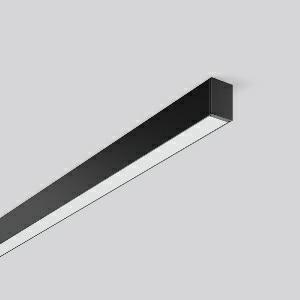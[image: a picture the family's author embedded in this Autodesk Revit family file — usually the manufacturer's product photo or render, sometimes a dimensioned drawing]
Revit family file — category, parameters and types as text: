
# Revit family: less_is_more_27_312198_003_1_76_4c85
name_source: partatom
category: Lighting Fixtures
units: mm (PartAtom-declared; Revit-internal decimal feet)

## family parameters
Cut with Voids When Loaded = No
Host = Face
Light Source = No
Part Type = Normal
Room Calculation Point = No
Round Connector Dimension = Use Diameter
Shared = No

## types (1)
- LESS IS MORE 27 (1 x LED Modul 840, 1900 lm, 4000)
    Apparent Load = 31 VA
    CIE Flux Codes = 48 79 96 100 100
    Color Rendering = 80
    Color Temperature = 4000
    Default Elevation = 1800 mm
    Description = Series: LESS IS MORE 27
Ceiling and wall luminaire with slim design. Housing: extruded aluminium profile, powder-coated. End cap aluminium powder-coated. Diffuser made of non-yellowing plastic (PMMA), opal. Suitable for Ceiling mounting, Wall (surface). External driver with connecting cable. 
Colour: deep black, matt (RAL 9005)
Length: 1212 mm
Width: 28 mm
Height: 38 mm
Lamp: LED
Socket: without socket
Colour temperature: 4000K
Colour rendering index (CRI): 82
System power: 31 W
Rated luminous flux: 1900 lm
Luminous efficiency: 61 lm/W
Control gear: Voltage converter, DALI dim.
Protection class: II
Type of protection: IP 20
    Height = 38 mm
    Lamp = 1 x LED Modul 840
    Lamp Light Flux = 1900 lm
    Lamp count = 1
    Length = 1212 mm
    Lifetime = 50000 h
    Luminous efficacy = 61 lm/W
    Manufacturer = RZB
    ModVariant = No
    Model = 312198.003.1.76
    Mounting Place = Ceiling, Wall
    Mounting Type = Surface mounted
    Number of Poles = 1
    OnlyDefault = Yes
    Power Factor = 1
    Product Name = LESS IS MORE 27
    Product group = Surface mounted LED linear luminaires
    ProductGroupID = 307
    Protection Class = Protection class II
    Protection Degree = IP 20
    RLX_Detail_Level = 1
    RLX_Emergency_Light_Flux = 0 lm
    RLX_Emergency_Type = 0
    RLX_Emergency_Type_DB = No
    RlxData = <blob elided: 28709 chars, md5=24ffebfc>
    Socket = socket
    Standby Power = 0 W
    System Light Flux = 1900 lm
    System Power = 31 W
    Type Comments = Product without accessories
    Type Image = 312196.003.jpg
    URL = http://relux.com
    VarID = ---
    Voltage = 230 V
    Voltage Range = 220-240 V
    Weight = 0.00 kg
    Width = 28 mm

## geometry (parser evidence)
native form markers: Blend x4, Sweep x10
no freeform markers — native parametric forms only
